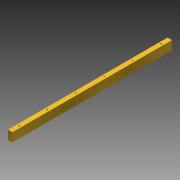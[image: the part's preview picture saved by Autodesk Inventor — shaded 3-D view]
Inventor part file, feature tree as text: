
AUTODESK INVENTOR PART (.ipt)
format: ipt  version: 2016 (Build 200138000, 138)  size: 119,296 bytes
history: native  units: in
note: dims shown in document units (in); Inventor stores cm internally (conversion verified against a paired STEP export)
features: sketch x3, hole x3, pattern_linear x2, extrude x1
ambient origin geometry x8: Origin, YZ Plane, XZ Plane, XY Plane, X Axis, Y Axis, Z Axis, Center Point
bodies: Solid1 (feature_tree)
feature tree (9):
  extrude  "Extrusion1"  Depth=0.5in
  sketch  "Sketch3"  dims[d6=9.0in d7=0.0in d8=0.3703in]
  hole  "Hole1"  [1 undecoded]
  pattern_linear  "Rectangular Pattern1"  Count1=4 Spacing1=1.0in
  hole  "Hole5"  [1 undecoded]
  hole  "Hole6"  [1 undecoded]
  pattern_linear  "Rectangular Pattern5"  Spacing1=0.5in  [1 undecoded]
  sketch  "Sketch2"  dims[d3=0.25in d5=0.5in]
  sketch  "Sketch7"  dims[d9=0.7in d10=0.067in d11=0.75in d12=0.375in d13=0.25in d14=0.5635in d15=1.0in d16=0.8108in d17=1.5748in d19=1.0in d60=8.2in d61=0.3703in d62=0.067in d63=0.75in d64=0.375in d65=0.25in d66=0.5635in d67=1.0in d68=0.8108in d69=0.5in d70=0.125in d71=0.067in d72=0.75in d73=0.375in d74=0.25in d75=0.5635in d76=0.25in d77=0.8108in d78=2.3622in d80=1.6in]
note: 4 required parameter values undecoded (feature->parameter linkage not recoverable at this tier; creation-order binding heuristic only, values carry confidence <= 0.55)
